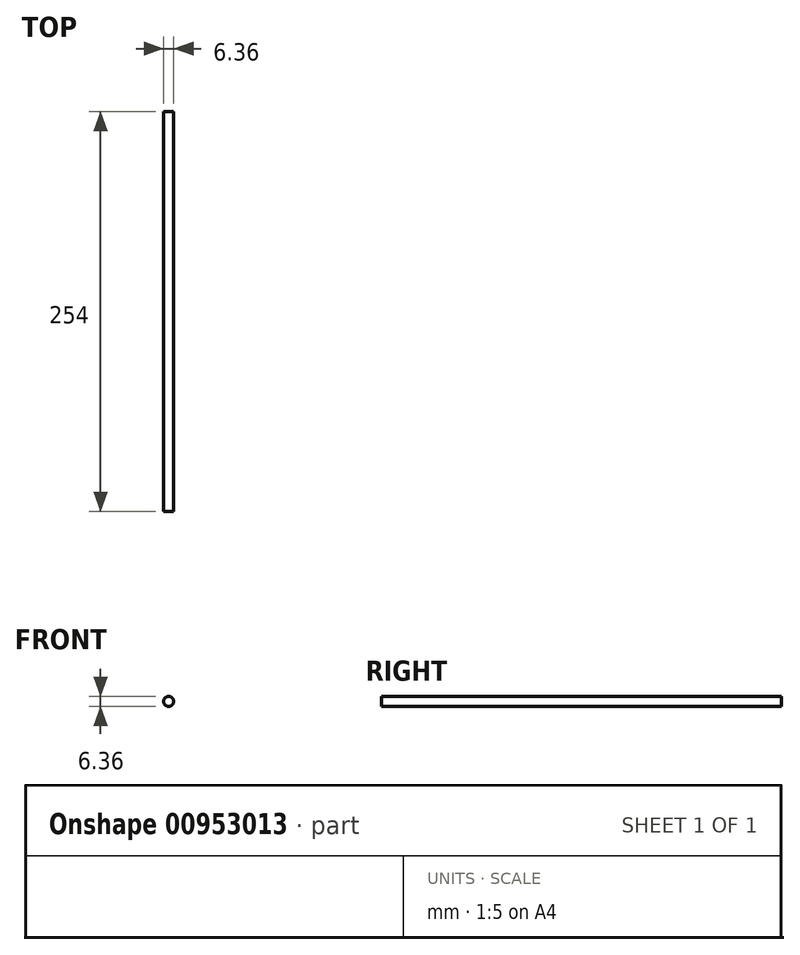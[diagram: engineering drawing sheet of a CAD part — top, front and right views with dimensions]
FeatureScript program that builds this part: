
annotation { "Feature Type Name" : "Feature", "Feature Type Description" : "" }
export const myFeature = defineFeature(function(context is Context, id is Id, definition is map)
    precondition{}
    {
        {
            var Q0;
            Q0=qCreatedBy(makeId("Front.planeOp"),FACE);
            var sketch = newSketch(context, id + "F0", { "sketchPlane" : qUnion([Q0])});
            skCircle(sketch, "E0", {"center": v(0, 0) * mm, "radius": 3.18 * mm});
            skSolve(sketch);
        }
        {
            var Q0;
            Q0=makeQuery(id+"F0.imprint","IMPRINT",FACE,{"disambiguationData":[TD([[makeQuery(id+"F0.imprint","IMPRINT",EDGE,{"derivedFrom":sQuery(id+"F0.wireOp",EDGE,"E0")}),1.0]])]});
            extrude(context, id + "F1", {"entities" : qUnion([Q0]), "depth" : 254 * mm, "offsetDistance" : 25.4 * mm});
        }
    });
